# Revit family: 926-12-002-DN50-1000
name_source: partatom
category: Pipe Accessories
units: mm (PartAtom-declared; Revit-internal decimal feet)

## family parameters
Always vertical = Yes
Cut with Voids When Loaded = No
Part Type = Valve - Breaks Into
Round Connector Dimension = Use Diameter
Shared = No
Work Plane-Based = No

## types (14) — shared parameters
Search_table = 926-12-002-DN50-1000
URL_product_pages = https://www.avkvalves.com
zero-valued in all types: Default Elevation

## per-type parameters (varying)
- DN1000_PN25: A=216 mm; B=700 mm; Body_T=20 mm  [stored 0.0656168 ft]; Body_end_shaft_R=99 mm; Body_rib_L=115 mm; Body_rib_W=55 mm; Body_shaft_R1=84 mm; Body_shaft_R2=58 mm; Body_shaft_R2_T=60 mm; Body_shaft_R3=75 mm; Body_shaft_R3_T=33 mm  [stored 0.108268 ft]; Bore_R=500 mm; C=856 mm; D=75 mm; DN=1000 mm; DN050_PN25=926-050-12-030160100000; DN080_PN25=926-080-12-030160100000; DN1000_PN25=926-A10-12-030060100000; DN100_PN25=926-100-12-030160100000; DN150_PN25=926-150-12-030080100000; DN200_PN25=926-200-12-030080100000; DN250_PN25=926-250-12-030080100000; DN300_PN25=926-300-12-030080100000; DN350_PN25=926-350-12-030080100000; DN400_PN25=926-400-12-030080100000; DN450_PN25=926-450-12-030080100000; DN500_PN25=926-500-12-030080100000; DN600_PN25=926-600-12-030080100000; DN700_PN25=926-700-12-030060100000; Description_=AVK DBL. ECC. BUTTERFLY VALVE, WAFER, API609B, PN25; E=80 mm; FL_R=522 mm; FL_T=40 mm  [stored 0.131234 ft]; Hole_R=19 mm  [stored 0.062336 ft]; L=8 mm  [stored 0.0262467 ft]; PCD=1160 mm; Raised_R=556 mm; Raised_dis=5 mm  [stored 0.0164042 ft]; Rib_R=38 mm  [stored 0.124672 ft]; Rib_T=23 mm  [stored 0.0754593 ft]; Seal_R=11 mm  [stored 0.0360892 ft]; Slot_T=22 mm  [stored 0.0721785 ft]; Slot_dim1=15 mm  [stored 0.0492126 ft]; Top _Flange_dim1=51 mm; Top _Flange_dim2=66 mm; Top_Flange_R=175 mm; Top_Rib=38 mm  [stored 0.124672 ft]; Wedge=166 mm; bottom_Shaft_R=78 mm; bottom_Shaft_T=39 mm  [stored 0.127953 ft]; logo=522 mm; rib_Loctn=46 mm; total_FL_legth=209 mm
- DN050_PN25: A=43 mm; B=80 mm; Body_T=8 mm  [stored 0.0262467 ft]; Body_end_shaft_R=18 mm  [stored 0.0590551 ft]; Body_rib_L=15 mm  [stored 0.0492126 ft]; Body_rib_W=8 mm  [stored 0.0262467 ft]; Body_shaft_R1=16 mm  [stored 0.0524934 ft]; Body_shaft_R2=8 mm  [stored 0.0262467 ft]; Body_shaft_R2_T=7 mm  [stored 0.0229659 ft]; Body_shaft_R3=10 mm  [stored 0.0328084 ft]; Body_shaft_R3_T=4 mm  [stored 0.0131234 ft]; Bore_R=25 mm  [stored 0.082021 ft]; C=110 mm; D=9 mm  [stored 0.0295276 ft]; DN=50 mm; DN050_PN25=926-050-12-020140100000; DN080_PN25=926-A10-12-020140100000; DN1000_PN25=926-A10-12-020140100000; DN100_PN25=926-100-12-020140100000; DN150_PN25=926-150-12-020040100000; DN200_PN25=926-200-12-010040100000; DN250_PN25=926-250-12-010040100000; DN300_PN25=926-300-12-010040100000; DN350_PN25=926-350-12-010040100000; DN400_PN25=926-400-12-010040100000; DN450_PN25=926-450-12-010040100000; DN500_PN25=926-500-12-010040100000; DN600_PN25=926-600-12-020040100000; DN700_PN25=926-700-12-020040100000; Description_=AVK DBL. ECC. BUTTERFLY VALVE, WAFER, API609B, PN10/16; E=18 mm  [stored 0.0590551 ft]; FL_R=45 mm; FL_T=8 mm  [stored 0.0262467 ft]; Hole_R=4 mm  [stored 0.0131234 ft]; L=3 mm  [stored 0.00984252 ft]; PCD=120 mm; Raised_R=50 mm; Raised_dis=2 mm  [stored 0.00656168 ft]; Rib_R=5 mm  [stored 0.0164042 ft]; Rib_T=4 mm  [stored 0.0131234 ft]; Seal_R=10 mm  [stored 0.0328084 ft]; Slot_T=6 mm  [stored 0.019685 ft]; Slot_dim1=4 mm  [stored 0.0131234 ft]; Top _Flange_dim1=7 mm  [stored 0.0229659 ft]; Top _Flange_dim2=8 mm  [stored 0.0262467 ft]; Top_Flange_R=45 mm; Top_Rib=5 mm  [stored 0.0164042 ft]; Wedge=33 mm  [stored 0.108268 ft]; bottom_Shaft_R=10 mm  [stored 0.0328084 ft]; bottom_Shaft_T=6 mm  [stored 0.019685 ft]; logo=35 mm  [stored 0.114829 ft]; rib_Loctn=6 mm  [stored 0.019685 ft]; total_FL_legth=40 mm  [stored 0.131234 ft]
- DN080_PN25: A=46 mm; B=110 mm; Body_T=8 mm  [stored 0.0262467 ft]; Body_end_shaft_R=20 mm  [stored 0.0656168 ft]; Body_rib_L=20 mm  [stored 0.0656168 ft]; Body_rib_W=12 mm  [stored 0.0393701 ft]; Body_shaft_R1=18 mm  [stored 0.0590551 ft]; Body_shaft_R2=10 mm  [stored 0.0328084 ft]; Body_shaft_R2_T=7 mm  [stored 0.0229659 ft]; Body_shaft_R3=13 mm  [stored 0.0426509 ft]; Body_shaft_R3_T=4 mm  [stored 0.0131234 ft]; Bore_R=40 mm  [stored 0.131234 ft]; C=185 mm; D=9 mm  [stored 0.0295276 ft]; DN=80 mm; DN050_PN25=926-050-12-020140100000; DN080_PN25=926-A10-12-020140100000; DN1000_PN25=926-A10-12-020140100000; DN100_PN25=926-100-12-020140100000; DN150_PN25=926-150-12-020040100000; DN200_PN25=926-200-12-010040100000; DN250_PN25=926-250-12-010040100000; DN300_PN25=926-300-12-010040100000; DN350_PN25=926-350-12-010040100000; DN400_PN25=926-400-12-010040100000; DN450_PN25=926-450-12-010040100000; DN500_PN25=926-500-12-010040100000; DN600_PN25=926-600-12-020040100000; DN700_PN25=926-700-12-020040100000; Description_=AVK DBL. ECC. BUTTERFLY VALVE, WAFER, API609B, PN10/16; E=18 mm  [stored 0.0590551 ft]; FL_R=72 mm; FL_T=8 mm  [stored 0.0262467 ft]; Hole_R=5 mm  [stored 0.0164042 ft]; L=3 mm  [stored 0.00984252 ft]; PCD=160 mm; Raised_R=66 mm; Raised_dis=2 mm  [stored 0.00656168 ft]; Rib_R=5 mm  [stored 0.0164042 ft]; Rib_T=4 mm  [stored 0.0131234 ft]; Seal_R=16 mm  [stored 0.0524934 ft]; Slot_T=11 mm  [stored 0.0360892 ft]; Slot_dim1=15 mm  [stored 0.0492126 ft]; Top _Flange_dim1=9 mm  [stored 0.0295276 ft]; Top _Flange_dim2=20 mm  [stored 0.0656168 ft]; Top_Flange_R=45 mm; Top_Rib=5 mm  [stored 0.0164042 ft]; Wedge=35 mm  [stored 0.114829 ft]; bottom_Shaft_R=14 mm  [stored 0.0459318 ft]; bottom_Shaft_T=8 mm  [stored 0.0262467 ft]; logo=50 mm; rib_Loctn=8 mm  [stored 0.0262467 ft]; total_FL_legth=43 mm
- DN100_PN25: A=52 mm; B=130 mm; Body_T=10 mm  [stored 0.0328084 ft]; Body_end_shaft_R=23 mm  [stored 0.0754593 ft]; Body_rib_L=25 mm  [stored 0.082021 ft]; Body_rib_W=15 mm  [stored 0.0492126 ft]; Body_shaft_R1=21 mm  [stored 0.0688976 ft]; Body_shaft_R2=13 mm  [stored 0.0426509 ft]; Body_shaft_R2_T=9 mm  [stored 0.0295276 ft]; Body_shaft_R3=16 mm  [stored 0.0524934 ft]; Body_shaft_R3_T=5 mm  [stored 0.0164042 ft]; Bore_R=50 mm; C=202 mm; D=11 mm  [stored 0.0360892 ft]; DN=100 mm; DN050_PN25=926-050-12-020140100000; DN080_PN25=926-A10-12-020140100000; DN1000_PN25=926-A10-12-020140100000; DN100_PN25=926-100-12-020140100000; DN150_PN25=926-150-12-020040100000; DN200_PN25=926-200-12-010040100000; DN250_PN25=926-250-12-010040100000; DN300_PN25=926-300-12-010040100000; DN350_PN25=926-350-12-010040100000; DN400_PN25=926-400-12-010040100000; DN450_PN25=926-450-12-010040100000; DN500_PN25=926-500-12-010040100000; DN600_PN25=926-600-12-020040100000; DN700_PN25=926-700-12-020040100000; Description_=AVK DBL. ECC. BUTTERFLY VALVE, WAFER, API609B, PN10/16; E=20 mm  [stored 0.0656168 ft]; FL_R=81 mm; FL_T=8 mm  [stored 0.0262467 ft]; Hole_R=6 mm  [stored 0.019685 ft]; L=3 mm  [stored 0.00984252 ft]; PCD=180 mm; Raised_R=78 mm; Raised_dis=2 mm  [stored 0.00656168 ft]; Rib_R=6 mm  [stored 0.019685 ft]; Rib_T=4 mm  [stored 0.0131234 ft]; Seal_R=16 mm  [stored 0.0524934 ft]; Slot_T=11 mm  [stored 0.0360892 ft]; Slot_dim1=15 mm  [stored 0.0492126 ft]; Top _Flange_dim1=11 mm  [stored 0.0360892 ft]; Top _Flange_dim2=20 mm  [stored 0.0656168 ft]; Top_Flange_R=45 mm; Top_Rib=6 mm  [stored 0.019685 ft]; Wedge=40 mm  [stored 0.131234 ft]; bottom_Shaft_R=17 mm  [stored 0.0557743 ft]; bottom_Shaft_T=11 mm  [stored 0.0360892 ft]; logo=62 mm; rib_Loctn=10 mm  [stored 0.0328084 ft]; total_FL_legth=49 mm
- DN150_PN25: A=56 mm; B=170 mm; Body_T=12 mm  [stored 0.0393701 ft]; Body_end_shaft_R=25 mm  [stored 0.082021 ft]; Body_rib_L=32 mm  [stored 0.104987 ft]; Body_rib_W=20 mm  [stored 0.0656168 ft]; Body_shaft_R1=22 mm  [stored 0.0721785 ft]; Body_shaft_R2=16 mm  [stored 0.0524934 ft]; Body_shaft_R2_T=14 mm  [stored 0.0459318 ft]; Body_shaft_R3=21 mm  [stored 0.0688976 ft]; Body_shaft_R3_T=7 mm  [stored 0.0229659 ft]; Bore_R=75 mm; C=280 mm; D=17 mm  [stored 0.0557743 ft]; DN=150 mm; DN050_PN25=926-050-12-020140100000; DN080_PN25=926-A10-12-020140100000; DN1000_PN25=926-A10-12-020140100000; DN100_PN25=926-100-12-020140100000; DN150_PN25=926-150-12-020040100000; DN200_PN25=926-200-12-010040100000; DN250_PN25=926-250-12-010040100000; DN300_PN25=926-300-12-010040100000; DN350_PN25=926-350-12-010040100000; DN400_PN25=926-400-12-010040100000; DN450_PN25=926-450-12-010040100000; DN500_PN25=926-500-12-010040100000; DN600_PN25=926-600-12-020040100000; DN700_PN25=926-700-12-020040100000; Description_=AVK DBL. ECC. BUTTERFLY VALVE, WAFER, API609B, PN10/16; E=27 mm  [stored 0.0885827 ft]; FL_R=108 mm; FL_T=10 mm  [stored 0.0328084 ft]; Hole_R=8 mm  [stored 0.0262467 ft]; L=3 mm  [stored 0.00984252 ft]; PCD=240 mm; Raised_R=106 mm; Raised_dis=2 mm  [stored 0.00656168 ft]; Rib_R=9 mm  [stored 0.0295276 ft]; Rib_T=5 mm  [stored 0.0164042 ft]; Seal_R=17 mm  [stored 0.0557743 ft]; Slot_T=19 mm  [stored 0.062336 ft]; Slot_dim1=18 mm  [stored 0.0590551 ft]; Top _Flange_dim1=14 mm  [stored 0.0459318 ft]; Top _Flange_dim2=25 mm  [stored 0.082021 ft]; Top_Flange_R=63 mm; Top_Rib=9 mm  [stored 0.0295276 ft]; Wedge=43 mm; bottom_Shaft_R=22 mm  [stored 0.0721785 ft]; bottom_Shaft_T=14 mm  [stored 0.0459318 ft]; logo=89 mm; rib_Loctn=13 mm  [stored 0.0426509 ft]; total_FL_legth=53 mm
- DN200_PN25: A=60 mm; B=200 mm; Body_T=12 mm  [stored 0.0393701 ft]; Body_end_shaft_R=25 mm  [stored 0.082021 ft]; Body_rib_L=52 mm; Body_rib_W=22 mm  [stored 0.0721785 ft]; Body_shaft_R1=18 mm  [stored 0.0590551 ft]; Body_shaft_R2=26 mm; Body_shaft_R2_T=18 mm  [stored 0.0590551 ft]; Body_shaft_R3=34 mm; Body_shaft_R3_T=10 mm  [stored 0.0328084 ft]; Bore_R=100 mm; C=320 mm; D=22 mm  [stored 0.0721785 ft]; DN=200 mm; DN050_PN25=926-050-12-020140100000; DN080_PN25=926-A10-12-020140100000; DN1000_PN25=926-A10-12-020140100000; DN100_PN25=926-100-12-020140100000; DN150_PN25=926-150-12-020040100000; DN200_PN25=926-200-12-010040100000; DN250_PN25=926-250-12-010040100000; DN300_PN25=926-300-12-010040100000; DN350_PN25=926-350-12-010040100000; DN400_PN25=926-400-12-010040100000; DN450_PN25=926-450-12-010040100000; DN500_PN25=926-500-12-010040100000; DN600_PN25=926-600-12-020040100000; DN700_PN25=926-700-12-020040100000; Description_=AVK DBL. ECC. BUTTERFLY VALVE, WAFER, API609B, PN10/16; E=30 mm  [stored 0.0984252 ft]; FL_R=133 mm; FL_T=20 mm  [stored 0.0656168 ft]; Hole_R=12 mm  [stored 0.0393701 ft]; L=5 mm  [stored 0.0164042 ft]; PCD=295 mm; Raised_R=133 mm; Raised_dis=3 mm  [stored 0.00984252 ft]; Rib_R=11 mm  [stored 0.0360892 ft]; Rib_T=11 mm  [stored 0.0360892 ft]; Seal_R=16 mm  [stored 0.0524934 ft]; Slot_T=15 mm  [stored 0.0492126 ft]; Slot_dim1=21 mm  [stored 0.0688976 ft]; Top _Flange_dim1=23 mm  [stored 0.0754593 ft]; Top _Flange_dim2=20 mm  [stored 0.0656168 ft]; Top_Flange_R=63 mm; Top_Rib=11 mm  [stored 0.0360892 ft]; Wedge=46 mm; bottom_Shaft_R=35 mm  [stored 0.114829 ft]; bottom_Shaft_T=15 mm  [stored 0.0492126 ft]; logo=114 mm; rib_Loctn=21 mm  [stored 0.0688976 ft]; total_FL_legth=56 mm
- DN250_PN25: A=68 mm; B=222 mm; Body_T=14 mm  [stored 0.0459318 ft]; Body_end_shaft_R=29 mm; Body_rib_L=56 mm; Body_rib_W=24 mm  [stored 0.0787402 ft]; Body_shaft_R1=21 mm  [stored 0.0688976 ft]; Body_shaft_R2=28 mm  [stored 0.0918635 ft]; Body_shaft_R2_T=22 mm  [stored 0.0721785 ft]; Body_shaft_R3=36 mm  [stored 0.11811 ft]; Body_shaft_R3_T=12 mm  [stored 0.0393701 ft]; Bore_R=125 mm; C=340 mm; D=27 mm  [stored 0.0885827 ft]; DN=250 mm; DN050_PN25=926-050-12-020140100000; DN080_PN25=926-A10-12-020140100000; DN1000_PN25=926-A10-12-020140100000; DN100_PN25=926-100-12-020140100000; DN150_PN25=926-150-12-020040100000; DN200_PN25=926-200-12-010040100000; DN250_PN25=926-250-12-010040100000; DN300_PN25=926-300-12-010040100000; DN350_PN25=926-350-12-010040100000; DN400_PN25=926-400-12-010040100000; DN450_PN25=926-450-12-010040100000; DN500_PN25=926-500-12-010040100000; DN600_PN25=926-600-12-020040100000; DN700_PN25=926-700-12-020040100000; Description_=AVK DBL. ECC. BUTTERFLY VALVE, WAFER, API609B, PN10/16; E=36 mm  [stored 0.11811 ft]; FL_R=158 mm; FL_T=22 mm  [stored 0.0721785 ft]; Hole_R=12 mm  [stored 0.0393701 ft]; L=5 mm  [stored 0.0164042 ft]; PCD=350 mm; Raised_R=160 mm; Raised_dis=3 mm  [stored 0.00984252 ft]; Rib_R=14 mm  [stored 0.0459318 ft]; Rib_T=13 mm  [stored 0.0426509 ft]; Seal_R=16 mm  [stored 0.0524934 ft]; Slot_T=20 mm  [stored 0.0656168 ft]; Slot_dim1=6 mm  [stored 0.019685 ft]; Top _Flange_dim1=25 mm  [stored 0.082021 ft]; Top _Flange_dim2=24 mm  [stored 0.0787402 ft]; Top_Flange_R=75 mm; Top_Rib=14 mm  [stored 0.0459318 ft]; Wedge=52 mm; bottom_Shaft_R=38 mm  [stored 0.124672 ft]; bottom_Shaft_T=17 mm  [stored 0.0557743 ft]; logo=141 mm; rib_Loctn=22 mm  [stored 0.0721785 ft]; total_FL_legth=64 mm
- DN300_PN25: A=78 mm; B=260 mm; Body_T=14 mm  [stored 0.0459318 ft]; Body_end_shaft_R=32 mm  [stored 0.104987 ft]; Body_rib_L=60 mm; Body_rib_W=30 mm  [stored 0.0984252 ft]; Body_shaft_R1=24 mm  [stored 0.0787402 ft]; Body_shaft_R2=30 mm  [stored 0.0984252 ft]; Body_shaft_R2_T=22 mm  [stored 0.0721785 ft]; Body_shaft_R3=39 mm  [stored 0.127953 ft]; Body_shaft_R3_T=12 mm  [stored 0.0393701 ft]; Bore_R=150 mm; C=390 mm; D=27 mm  [stored 0.0885827 ft]; DN=300 mm; DN050_PN25=926-050-12-020140100000; DN080_PN25=926-A10-12-020140100000; DN1000_PN25=926-A10-12-020140100000; DN100_PN25=926-100-12-020140100000; DN150_PN25=926-150-12-020040100000; DN200_PN25=926-200-12-010040100000; DN250_PN25=926-250-12-010040100000; DN300_PN25=926-300-12-010040100000; DN350_PN25=926-350-12-010040100000; DN400_PN25=926-400-12-010040100000; DN450_PN25=926-450-12-010040100000; DN500_PN25=926-500-12-010040100000; DN600_PN25=926-600-12-020040100000; DN700_PN25=926-700-12-020040100000; Description_=AVK DBL. ECC. BUTTERFLY VALVE, WAFER, API609B, PN10/16; E=41 mm; FL_R=180 mm; FL_T=25 mm  [stored 0.082021 ft]; Hole_R=12 mm  [stored 0.0393701 ft]; L=6 mm  [stored 0.019685 ft]; PCD=400 mm; Raised_R=185 mm; Raised_dis=4 mm  [stored 0.0131234 ft]; Rib_R=14 mm  [stored 0.0459318 ft]; Rib_T=14 mm  [stored 0.0459318 ft]; Seal_R=15 mm  [stored 0.0492126 ft]; Slot_T=20 mm  [stored 0.0656168 ft]; Slot_dim1=6 mm  [stored 0.019685 ft]; Top _Flange_dim1=27 mm  [stored 0.0885827 ft]; Top _Flange_dim2=24 mm  [stored 0.0787402 ft]; Top_Flange_R=75 mm; Top_Rib=14 mm  [stored 0.0459318 ft]; Wedge=60 mm; bottom_Shaft_R=41 mm; bottom_Shaft_T=21 mm  [stored 0.0688976 ft]; logo=166 mm; rib_Loctn=24 mm  [stored 0.0787402 ft]; total_FL_legth=72 mm
- DN350_PN25: A=78 mm; B=290 mm; Body_T=14 mm  [stored 0.0459318 ft]; Body_end_shaft_R=32 mm  [stored 0.104987 ft]; Body_rib_L=67 mm; Body_rib_W=31 mm  [stored 0.101706 ft]; Body_shaft_R1=24 mm  [stored 0.0787402 ft]; Body_shaft_R2=34 mm; Body_shaft_R2_T=29 mm; Body_shaft_R3=44 mm; Body_shaft_R3_T=16 mm  [stored 0.0524934 ft]; Bore_R=175 mm; C=420 mm; D=36 mm  [stored 0.11811 ft]; DN=350 mm; DN050_PN25=926-050-12-020140100000; DN080_PN25=926-A10-12-020140100000; DN1000_PN25=926-A10-12-020140100000; DN100_PN25=926-100-12-020140100000; DN150_PN25=926-150-12-020040100000; DN200_PN25=926-200-12-010040100000; DN250_PN25=926-250-12-010040100000; DN300_PN25=926-300-12-010040100000; DN350_PN25=926-350-12-010040100000; DN400_PN25=926-400-12-010040100000; DN450_PN25=926-450-12-010040100000; DN500_PN25=926-500-12-010040100000; DN600_PN25=926-600-12-020040100000; DN700_PN25=926-700-12-020040100000; Description_=AVK DBL. ECC. BUTTERFLY VALVE, WAFER, API609B, PN10/16; E=41 mm; FL_R=207 mm; FL_T=25 mm  [stored 0.082021 ft]; Hole_R=12 mm  [stored 0.0393701 ft]; L=6 mm  [stored 0.019685 ft]; PCD=460 mm; Raised_R=215 mm; Raised_dis=4 mm  [stored 0.0131234 ft]; Rib_R=18 mm  [stored 0.0590551 ft]; Rib_T=14 mm  [stored 0.0459318 ft]; Seal_R=16 mm  [stored 0.0524934 ft]; Slot_T=22 mm  [stored 0.0721785 ft]; Slot_dim1=7 mm  [stored 0.0229659 ft]; Top _Flange_dim1=30 mm  [stored 0.0984252 ft]; Top _Flange_dim2=32 mm  [stored 0.104987 ft]; Top_Flange_R=75 mm; Top_Rib=18 mm  [stored 0.0590551 ft]; Wedge=60 mm; bottom_Shaft_R=46 mm; bottom_Shaft_T=22 mm  [stored 0.0721785 ft]; logo=191 mm; rib_Loctn=27 mm  [stored 0.0885827 ft]; total_FL_legth=72 mm
- DN400_PN25: A=102 mm; B=350 mm; Body_T=15 mm  [stored 0.0492126 ft]; Body_end_shaft_R=44 mm; Body_rib_L=70 mm; Body_rib_W=42 mm; Body_shaft_R1=36 mm  [stored 0.11811 ft]; Body_shaft_R2=35 mm  [stored 0.114829 ft]; Body_shaft_R2_T=29 mm; Body_shaft_R3=46 mm; Body_shaft_R3_T=16 mm  [stored 0.0524934 ft]; Bore_R=200 mm; C=451 mm; D=36 mm  [stored 0.11811 ft]; DN=400 mm; DN050_PN25=926-050-12-020140100000; DN080_PN25=926-A10-12-020140100000; DN1000_PN25=926-A10-12-020140100000; DN100_PN25=926-100-12-020140100000; DN150_PN25=926-150-12-020040100000; DN200_PN25=926-200-12-010040100000; DN250_PN25=926-250-12-010040100000; DN300_PN25=926-300-12-010040100000; DN350_PN25=926-350-12-010040100000; DN400_PN25=926-400-12-010040100000; DN450_PN25=926-450-12-010040100000; DN500_PN25=926-500-12-010040100000; DN600_PN25=926-600-12-020040100000; DN700_PN25=926-700-12-020040100000; Description_=AVK DBL. ECC. BUTTERFLY VALVE, WAFER, API609B, PN10/16; E=41 mm; FL_R=232 mm; FL_T=25 mm  [stored 0.082021 ft]; Hole_R=14 mm  [stored 0.0459318 ft]; L=6 mm  [stored 0.019685 ft]; PCD=515 mm; Raised_R=240 mm; Raised_dis=4 mm  [stored 0.0131234 ft]; Rib_R=18 mm  [stored 0.0590551 ft]; Rib_T=14 mm  [stored 0.0459318 ft]; Seal_R=16 mm  [stored 0.0524934 ft]; Slot_T=22 mm  [stored 0.0721785 ft]; Slot_dim1=7 mm  [stored 0.0229659 ft]; Top _Flange_dim1=31 mm  [stored 0.101706 ft]; Top _Flange_dim2=32 mm  [stored 0.104987 ft]; Top_Flange_R=88 mm; Top_Rib=18 mm  [stored 0.0590551 ft]; Wedge=78 mm; bottom_Shaft_R=48 mm; bottom_Shaft_T=29 mm; logo=217 mm; rib_Loctn=28 mm  [stored 0.0918635 ft]; total_FL_legth=96 mm
- DN450_PN25: A=114 mm; B=360 mm; Body_T=16 mm  [stored 0.0524934 ft]; Body_end_shaft_R=50 mm; Body_rib_L=78 mm; Body_rib_W=41 mm; Body_shaft_R1=41 mm; Body_shaft_R2=39 mm  [stored 0.127953 ft]; Body_shaft_R2_T=29 mm; Body_shaft_R3=51 mm; Body_shaft_R3_T=16 mm  [stored 0.0524934 ft]; Bore_R=225 mm; C=492 mm; D=36 mm  [stored 0.11811 ft]; DN=450 mm; DN050_PN25=926-050-12-020140100000; DN080_PN25=926-A10-12-020140100000; DN1000_PN25=926-A10-12-020140100000; DN100_PN25=926-100-12-020140100000; DN150_PN25=926-150-12-020040100000; DN200_PN25=926-200-12-010040100000; DN250_PN25=926-250-12-010040100000; DN300_PN25=926-300-12-010040100000; DN350_PN25=926-350-12-010040100000; DN400_PN25=926-400-12-010040100000; DN450_PN25=926-450-12-010040100000; DN500_PN25=926-500-12-010040100000; DN600_PN25=926-600-12-020040100000; DN700_PN25=926-700-12-020040100000; Description_=AVK DBL. ECC. BUTTERFLY VALVE, WAFER, API609B, PN10/16; E=38 mm  [stored 0.124672 ft]; FL_R=254 mm; FL_T=26 mm; Hole_R=14 mm  [stored 0.0459318 ft]; L=6 mm  [stored 0.019685 ft]; PCD=565 mm; Raised_R=265 mm; Raised_dis=4 mm  [stored 0.0131234 ft]; Rib_R=18 mm  [stored 0.0590551 ft]; Rib_T=14 mm  [stored 0.0459318 ft]; Seal_R=15 mm  [stored 0.0492126 ft]; Slot_T=22 mm  [stored 0.0721785 ft]; Slot_dim1=7 mm  [stored 0.0229659 ft]; Top _Flange_dim1=34 mm; Top _Flange_dim2=32 mm  [stored 0.104987 ft]; Top_Flange_R=105 mm; Top_Rib=18 mm  [stored 0.0590551 ft]; Wedge=88 mm; bottom_Shaft_R=53 mm; bottom_Shaft_T=29 mm; logo=243 mm; rib_Loctn=31 mm  [stored 0.101706 ft]; total_FL_legth=108 mm
- DN500_PN25: A=127 mm; B=380 mm; Body_T=15 mm  [stored 0.0492126 ft]; Body_end_shaft_R=57 mm; Body_rib_L=87 mm; Body_rib_W=38 mm  [stored 0.124672 ft]; Body_shaft_R1=47 mm; Body_shaft_R2=44 mm; Body_shaft_R2_T=37 mm; Body_shaft_R3=57 mm; Body_shaft_R3_T=20 mm  [stored 0.0656168 ft]; Bore_R=250 mm; C=511 mm; D=46 mm; DN=500 mm; DN050_PN25=926-050-12-020140100000; DN080_PN25=926-A10-12-020140100000; DN1000_PN25=926-A10-12-020140100000; DN100_PN25=926-100-12-020140100000; DN150_PN25=926-150-12-020040100000; DN200_PN25=926-200-12-010040100000; DN250_PN25=926-250-12-010040100000; DN300_PN25=926-300-12-010040100000; DN350_PN25=926-350-12-010040100000; DN400_PN25=926-400-12-010040100000; DN450_PN25=926-450-12-010040100000; DN500_PN25=926-500-12-010040100000; DN600_PN25=926-600-12-020040100000; DN700_PN25=926-700-12-020040100000; Description_=AVK DBL. ECC. BUTTERFLY VALVE, WAFER, API609B, PN10/16; E=65 mm; FL_R=279 mm; FL_T=27 mm  [stored 0.0885827 ft]; Hole_R=14 mm  [stored 0.0459318 ft]; L=6 mm  [stored 0.019685 ft]; PCD=620 mm; Raised_R=291 mm; Raised_dis=4 mm  [stored 0.0131234 ft]; Rib_R=23 mm  [stored 0.0754593 ft]; Rib_T=15 mm  [stored 0.0492126 ft]; Seal_R=15 mm  [stored 0.0492126 ft]; Slot_T=22 mm  [stored 0.0721785 ft]; Slot_dim1=9 mm  [stored 0.0295276 ft]; Top _Flange_dim1=38 mm  [stored 0.124672 ft]; Top _Flange_dim2=40 mm  [stored 0.131234 ft]; Top_Flange_R=105 mm; Top_Rib=23 mm  [stored 0.0754593 ft]; Wedge=98 mm; bottom_Shaft_R=59 mm; bottom_Shaft_T=27 mm  [stored 0.0885827 ft]; logo=267 mm; rib_Loctn=35 mm  [stored 0.114829 ft]; total_FL_legth=121 mm
- DN600_PN25: A=154 mm; B=450 mm; Body_T=17 mm  [stored 0.0557743 ft]; Body_end_shaft_R=68 mm; Body_rib_L=97 mm; Body_rib_W=45 mm; Body_shaft_R1=58 mm; Body_shaft_R2=49 mm; Body_shaft_R2_T=44 mm; Body_shaft_R3=63 mm; Body_shaft_R3_T=24 mm  [stored 0.0787402 ft]; Bore_R=300 mm; C=561 mm; D=55 mm; DN=600 mm; DN050_PN25=926-050-12-020140100000; DN080_PN25=926-A10-12-020140100000; DN1000_PN25=926-A10-12-020140100000; DN100_PN25=926-100-12-020140100000; DN150_PN25=926-150-12-020040100000; DN200_PN25=926-200-12-010040100000; DN250_PN25=926-250-12-010040100000; DN300_PN25=926-300-12-010040100000; DN350_PN25=926-350-12-010040100000; DN400_PN25=926-400-12-010040100000; DN450_PN25=926-450-12-010040100000; DN500_PN25=926-500-12-010040100000; DN600_PN25=926-600-12-020040100000; DN700_PN25=926-700-12-020040100000; Description_=AVK DBL. ECC. BUTTERFLY VALVE, WAFER, API609B, PN10/16; E=70 mm; FL_R=326 mm; FL_T=30 mm  [stored 0.0984252 ft]; Hole_R=16 mm  [stored 0.0524934 ft]; L=8 mm  [stored 0.0262467 ft]; PCD=725 mm; Raised_R=341 mm; Raised_dis=5 mm  [stored 0.0164042 ft]; Rib_R=28 mm  [stored 0.0918635 ft]; Rib_T=17 mm  [stored 0.0557743 ft]; Seal_R=13 mm  [stored 0.0426509 ft]; Slot_T=15 mm  [stored 0.0492126 ft]; Slot_dim1=11 mm  [stored 0.0360892 ft]; Top _Flange_dim1=43 mm; Top _Flange_dim2=48 mm; Top_Flange_R=150 mm; Top_Rib=28 mm  [stored 0.0918635 ft]; Wedge=118 mm; bottom_Shaft_R=66 mm; bottom_Shaft_T=32 mm  [stored 0.104987 ft]; logo=319 mm; rib_Loctn=39 mm  [stored 0.127953 ft]; total_FL_legth=147 mm
- DN700_PN25: A=165 mm; B=500 mm; Body_T=18 mm  [stored 0.0590551 ft]; Body_end_shaft_R=74 mm; Body_rib_L=105 mm; Body_rib_W=40 mm  [stored 0.131234 ft]; Body_shaft_R1=63 mm; Body_shaft_R2=53 mm; Body_shaft_R2_T=64 mm; Body_shaft_R3=68 mm; Body_shaft_R3_T=30 mm  [stored 0.0984252 ft]; Bore_R=350 mm; C=655 mm; D=80 mm; DN=700 mm; DN050_PN25=926-050-12-030160100000; DN080_PN25=926-A10-12-030160100000; DN1000_PN25=926-A10-12-030160100000; DN100_PN25=926-100-12-030160100000; DN150_PN25=926-150-12-030080100000; DN200_PN25=926-200-12-030080100000; DN250_PN25=926-250-12-030080100000; DN300_PN25=926-300-12-030080100000; DN350_PN25=926-350-12-030080100000; DN400_PN25=926-400-12-030080100000; DN450_PN25=926-450-12-030080100000; DN500_PN25=926-500-12-030080100000; DN600_PN25=926-600-12-030080100000; DN700_PN25=926-700-12-030060100000; Description_=AVK DBL. ECC. BUTTERFLY VALVE, WAFER, API609B, PN25; E=110 mm; FL_R=378 mm; FL_T=33 mm  [stored 0.108268 ft]; Hole_R=16 mm  [stored 0.0524934 ft]; L=8 mm  [stored 0.0262467 ft]; PCD=840 mm; Raised_R=397 mm; Raised_dis=5 mm  [stored 0.0164042 ft]; Rib_R=40 mm  [stored 0.131234 ft]; Rib_T=18 mm  [stored 0.0590551 ft]; Seal_R=14 mm  [stored 0.0459318 ft]; Slot_T=15 mm  [stored 0.0492126 ft]; Slot_dim1=16 mm  [stored 0.0524934 ft]; Top _Flange_dim1=46 mm; Top _Flange_dim2=58 mm; Top_Flange_R=150 mm; Top_Rib=40 mm  [stored 0.131234 ft]; Wedge=127 mm; bottom_Shaft_R=71 mm; bottom_Shaft_T=28 mm  [stored 0.0918635 ft]; logo=370 mm; rib_Loctn=42 mm; total_FL_legth=158 mm

note: [stored X ft] marks values corroborated as IEEE doubles in the binary element streams (Revit-internal decimal feet)

## geometry (parser evidence)
native form markers: Sweep x17
no freeform markers — native parametric forms only
